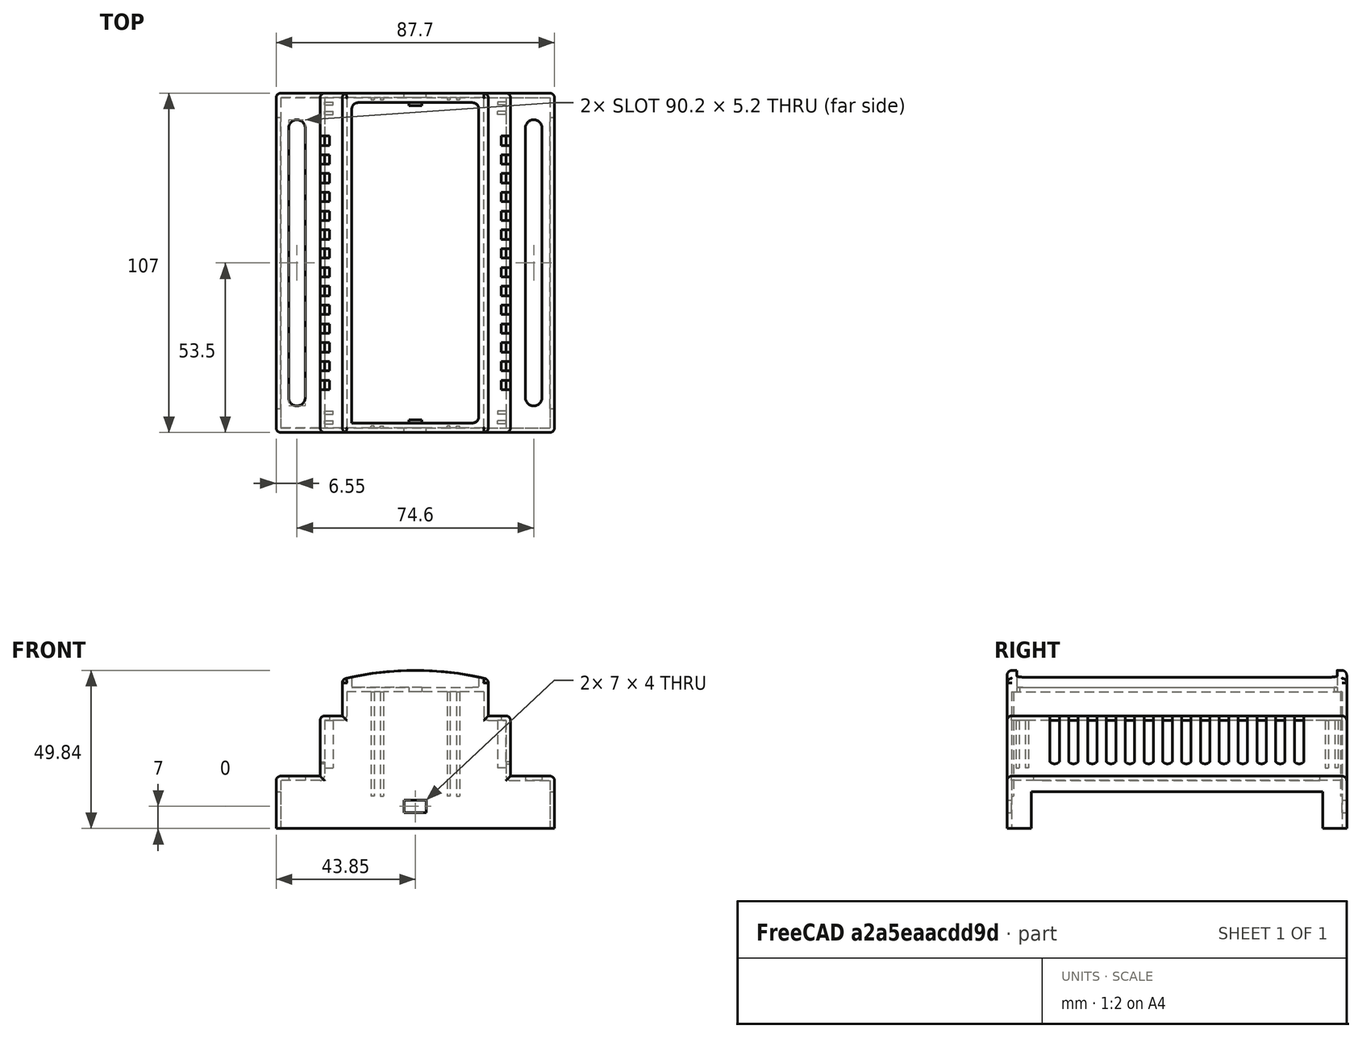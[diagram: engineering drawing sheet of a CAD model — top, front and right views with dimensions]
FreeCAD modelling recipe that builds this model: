
FCSTD DOCUMENT  (FreeCAD 1.0R39285 (Git))
Label: Diseño superior de la pieza (2023-1283)
License: All rights reserved
LicenseURL: https://en.wikipedia.org/wiki/All_rights_reserved
objects: Sketcher::SketchObject×15, PartDesign::Pad×9, PartDesign::Mirrored×7, PartDesign::Pocket×6, PartDesign::Fillet×4, PartDesign::Thickness×2, PartDesign::Plane×1, PartDesign::Body×1
note: 109 computed .brp shape members not serialized (recipe doc carries the construction recipe); baked Part::Feature solids carry a one-line shape summary decoded from their .brp

FEATURE [Sketcher::SketchObject] Sketch
  ArcFitTolerance = 1e-06
  AttachmentSupport = -> [XZ_Plane001]
  FullyConstrained = true
  MakeInternals = false
  MapMode = 5
  Placement = pos=(0,0,0) rot=(1,0,0;1.5708rad)
  sketch-geometry (12):
    g0: LineSegment StartX=-43.85 StartY=0 StartZ=0 EndX=43.85 EndY=0 EndZ=0
    g1: LineSegment StartX=-43.85 StartY=0 StartZ=0 EndX=-43.85 EndY=16.54 EndZ=0
    g2: LineSegment StartX=43.85 StartY=0 StartZ=0 EndX=43.85 EndY=16.54 EndZ=0
    g3: LineSegment StartX=-43.85 StartY=16.54 StartZ=0 EndX=-30 EndY=16.54 EndZ=0
    g4: LineSegment StartX=43.85 StartY=16.54 StartZ=0 EndX=30 EndY=16.54 EndZ=0
    g5: LineSegment StartX=-30 StartY=16.54 StartZ=0 EndX=-30 EndY=35.54 EndZ=0
    g6: LineSegment StartX=30 StartY=16.54 StartZ=0 EndX=30 EndY=35.54 EndZ=0
    g7: LineSegment StartX=-30 StartY=35.54 StartZ=0 EndX=-23 EndY=35.54 EndZ=0
    g8: LineSegment StartX=30 StartY=35.54 StartZ=0 EndX=23 EndY=35.54 EndZ=0
    g9: LineSegment StartX=23 StartY=35.54 StartZ=0 EndX=23 EndY=44.54 EndZ=0
    g10: LineSegment StartX=-23 StartY=35.54 StartZ=0 EndX=-23 EndY=44.54 EndZ=0
    g11: LineSegment StartX=-23 StartY=44.54 StartZ=0 EndX=23 EndY=44.54 EndZ=0
  constraints (36):
    c: Distance(g0) = 87.7
    c: PointOnObject(g0,g-1)
    c: PointOnObject(g0,g-1)
    c: Vertical(g1)
    c: Coincident(g1,g0)
    c: Vertical(g2)
    c: Coincident(g2,g0)
    c: Distance(g3) = 13.85
    c: Horizontal(g3)
    c: Coincident(g3,g1)
    c: Distance(g4) = 13.85
    c: Horizontal(g4)
    c: Coincident(g4,g2)
    c: Vertical(g5)
    c: Coincident(g5,g3)
    c: Vertical(g6)
    c: Coincident(g6,g4)
    c: Distance(g7) = 7
    c: Horizontal(g7)
    c: Coincident(g7,g5)
    c: Distance(g8) = 7
    c: Horizontal(g8)
    c: Coincident(g8,g6)
    c: Vertical(g9)
    c: Coincident(g9,g8)
    c: Vertical(g10)
    c: Coincident(g10,g7)
    c: Coincident(g11,g10)
    c: Coincident(g11,g9)
    c: Equal(g1,g2)
    c: Equal(g5,g6)
    c: Equal(g10,g9)
    c: Distance(g0,g11) = 44.54
    c: DistanceY(g1,g1) = 16.54
    c: Distance(g5,g0) = 35.54
    c: Distance(g10,g-2) = 23
FEATURE [PartDesign::Pad] Pad
  Direction = (0,-1,2e-16)
  Length = 107
  Length2 = 10
  Placement = pos=(0,0,0) rot=(1,0,0;1.5708rad)
  Profile = -> Sketch
  ReferenceAxis = -> Sketch [N_Axis]
  Refine = true
  Suppressed = false
  Type = 0
FEATURE [PartDesign::Thickness] Thickness
  Base = -> Pad
  BaseFeature = -> Pad
  Intersection = false
  Join = 0
  Mode = 0
  Placement = pos=(0,0,0) rot=(1,0,0;1.5708rad)
  Refine = true
  Reversed = true
  SupportTransform = false
  Suppressed = false
  Value = 1.4
FEATURE [PartDesign::Thickness] Thickness001
  Base = -> Thickness [Face1]
  BaseFeature = -> Thickness
  Intersection = false
  Join = 0
  Mode = 0
  Refine = true
  Reversed = true
  SupportTransform = false
  Suppressed = false
  Value = 1.4
FEATURE [Sketcher::SketchObject] Sketch001
  ArcFitTolerance = 1e-06
  AttachmentSupport = -> [Thickness001]
  FullyConstrained = true
  MakeInternals = false
  MapMode = 5
  Placement = pos=(-43.85,0,0) rot=(0.57735,-0.57735,-0.57735;2.0944rad)
  sketch-geometry (4):
    g0: LineSegment StartX=7.575 StartY=0 StartZ=0 EndX=99.425 EndY=0 EndZ=0
    g1: LineSegment StartX=99.425 StartY=0 StartZ=0 EndX=99.425 EndY=11.6 EndZ=0
    g2: LineSegment StartX=99.425 StartY=11.6 StartZ=0 EndX=7.575 EndY=11.6 EndZ=0
    g3: LineSegment StartX=7.575 StartY=11.6 StartZ=0 EndX=7.575 EndY=0 EndZ=0
  constraints (12):
    c: Coincident(g0,g1)
    c: Coincident(g1,g2)
    c: Coincident(g2,g3)
    c: Coincident(g3,g0)
    c: Horizontal(g0)
    c: Horizontal(g2)
    c: Vertical(g1)
    c: Vertical(g3)
    c: PointOnObject(g0,g-1)
    c: DistanceX(g2,g2) = 91.85
    c: DistanceY(g1,g1) = 11.6
    c: DistanceX(g-1,g0) = 7.575
FEATURE [PartDesign::Pocket] Pocket
  BaseFeature = -> Thickness001
  Direction = (1,0,0)
  Length = 5
  Length2 = 5
  Profile = -> Sketch001
  ReferenceAxis = -> Sketch001 [N_Axis]
  Refine = true
  Suppressed = false
  Type = 1
FEATURE [Sketcher::SketchObject] Sketch002
  ArcFitTolerance = 1e-06
  AttachmentSupport = -> [Pocket]
  FullyConstrained = true
  MakeInternals = false
  MapMode = 5
  Placement = pos=(0,4.2e-15,0) rot=(0,0.707107,0.707107;3.14159rad)
  sketch-geometry (4):
    g0: LineSegment StartX=-23 StartY=44.54 StartZ=0 EndX=23 EndY=44.54 EndZ=0
    g1: LineSegment StartX=-23 StartY=44.54 StartZ=0 EndX=-23 EndY=47.04 EndZ=0
    g2: LineSegment StartX=23 StartY=44.54 StartZ=0 EndX=23 EndY=47.04 EndZ=0
    g3: ArcOfCircle CenterX=1.7e-15 CenterY=-46.0243 CenterZ=0 NormalX=0 NormalY=0 NormalZ=1 AngleXU=0 Radius=95.8643 StartAngle=1.32851 EndAngle=1.81308
  constraints (13):
    c: Distance(g0) = 46
    c: Horizontal(g0)
    c: Distance(g-1,g0) = 44.54
    c: Distance(g0,g-2) = 23
    c: Distance(g1) = 2.5
    c: Coincident(g1,g0)
    c: Vertical(g1)
    c: Distance(g2) = 2.5
    c: Coincident(g2,g0)
    c: Vertical(g2)
    c: Coincident(g3,g1)
    c: Coincident(g3,g2)
    c: Distance(g3,g0) = -5.3
FEATURE [PartDesign::Pad] Pad001
  BaseFeature = -> Pocket
  Direction = (0,1,-2e-16)
  Length = 107
  Length2 = 10
  Profile = -> Sketch002
  ReferenceAxis = -> Sketch002 [N_Axis]
  Refine = true
  Suppressed = false
  Type = 0
FEATURE [Sketcher::SketchObject] Sketch003
  ArcFitTolerance = 1e-06
  AttachmentSupport = -> [Pad001]
  ExternalGeometry = -> [Pad001]
  FullyConstrained = true
  MakeInternals = false
  MapMode = 5
  Placement = pos=(0,4.2e-15,0) rot=(0,0.707107,0.707107;3.14159rad)
  sketch-geometry (4):
    g0: LineSegment StartX=-23 StartY=44.54 StartZ=0 EndX=-23 EndY=47.04 EndZ=0
    g1: LineSegment StartX=23 StartY=44.54 StartZ=0 EndX=23 EndY=47.04 EndZ=0
    g2: ArcOfCircle CenterX=4.82e-14 CenterY=-46.0243 CenterZ=0 NormalX=0 NormalY=0 NormalZ=1 AngleXU=0 Radius=95.8643 StartAngle=1.32851 EndAngle=1.81308
    g3: LineSegment StartX=-23 StartY=44.54 StartZ=0 EndX=23 EndY=44.54 EndZ=0
  constraints (9):
    c: Distance(g0) = 2.5
    c: Coincident(g2,g0)
    c: Coincident(g2,g1)
    c: Coincident(g3,g-3)
    c: Coincident(g3,g-3)
    c: Perpendicular(g0,g3) = 4.71239
    c: Distance(g2,g3) = -5.3
    c: Perpendicular(g1,g3) = 4.71239
    c: DistanceY(g1,g1) = 2.5
FEATURE [PartDesign::Pad] Pad002
  BaseFeature = -> Pad001
  Direction = (0,1,-2e-16)
  Length = 3
  Length2 = 10
  Profile = -> Sketch003
  ReferenceAxis = -> Sketch003 [N_Axis]
  Refine = true
  Reversed = true
  Suppressed = false
  Type = 0
FEATURE [Sketcher::SketchObject] Sketch004
  ArcFitTolerance = 1e-06
  AttachmentSupport = -> [Pad002]
  ExternalGeometry = -> [Pad002]
  FullyConstrained = true
  MakeInternals = false
  MapMode = 5
  Placement = pos=(0,-107,0) rot=(1,0,0;1.5708rad)
  sketch-geometry (4):
    g0: LineSegment StartX=-23 StartY=44.54 StartZ=0 EndX=23 EndY=44.54 EndZ=0
    g1: LineSegment StartX=23 StartY=44.54 StartZ=0 EndX=23 EndY=47.04 EndZ=0
    g2: LineSegment StartX=-23 StartY=44.54 StartZ=0 EndX=-23 EndY=47.04 EndZ=0
    g3: ArcOfCircle CenterX=3.7756e-12 CenterY=-46.0243 CenterZ=0 NormalX=0 NormalY=0 NormalZ=1 AngleXU=0 Radius=95.8643 StartAngle=1.32851 EndAngle=1.81308
  constraints (9):
    c: Coincident(g0,g-5)
    c: Coincident(g0,g-6)
    c: Coincident(g1,g0)
    c: Coincident(g1,g-6)
    c: Coincident(g2,g0)
    c: Coincident(g2,g-5)
    c: Coincident(g3,g2)
    c: Coincident(g3,g1)
    c: Tangent(g3,g-4)
FEATURE [PartDesign::Pad] Pad003
  BaseFeature = -> Pad002
  Direction = (0,-1,2e-16)
  Length = 3
  Length2 = 10
  Profile = -> Sketch004
  ReferenceAxis = -> Sketch004 [N_Axis]
  Refine = true
  Reversed = true
  Suppressed = false
  Type = 0
FEATURE [Sketcher::SketchObject] Sketch005
  ArcFitTolerance = 1e-06
  AttachmentSupport = -> [Pad003]
  ExternalGeometry = -> [Pad003]
  FullyConstrained = true
  MakeInternals = false
  MapMode = 5
  Placement = pos=(23,-8.5e-15,1.304e-13) rot=(0.57735,0.57735,0.57735;2.0944rad)
  sketch-geometry (4):
    g0: LineSegment StartX=-104 StartY=49.84 StartZ=0 EndX=-104 EndY=44.54 EndZ=0
    g1: LineSegment StartX=-104 StartY=44.54 StartZ=0 EndX=-3 EndY=44.54 EndZ=0
    g2: LineSegment StartX=-3 StartY=49.84 StartZ=0 EndX=-3 EndY=44.54 EndZ=0
    g3: LineSegment StartX=-104 StartY=49.84 StartZ=0 EndX=-3 EndY=49.84 EndZ=0
  constraints (8):
    c: Coincident(g0,g-5)
    c: Coincident(g0,g-3)
    c: Coincident(g1,g0)
    c: Coincident(g1,g-3)
    c: Coincident(g2,g-4)
    c: Coincident(g2,g1)
    c: Coincident(g3,g0)
    c: Coincident(g3,g2)
FEATURE [PartDesign::Pad] Pad004
  BaseFeature = -> Pad003
  Direction = (1,0,5.8e-15)
  Length = 3
  Length2 = 10
  Profile = -> Sketch005
  ReferenceAxis = -> Sketch005 [N_Axis]
  Refine = true
  Reversed = true
  Suppressed = false
  Type = 0
FEATURE [PartDesign::Mirrored] Mirrored
  BaseFeature = -> Pad004
  MirrorPlane = -> YZ_Plane001
  Originals = -> [Pad004]
  Refine = true
  Suppressed = false
  TransformMode = 0
FEATURE [Sketcher::SketchObject] Sketch006
  ArcFitTolerance = 1e-06
  AttachmentSupport = -> [Mirrored]
  FullyConstrained = true
  MakeInternals = false
  MapMode = 5
  Placement = pos=(0,7.3e-15,16.54) rot=(0,0,1;0rad)
  sketch-geometry (4):
    g0: ArcOfCircle CenterX=37.3 CenterY=-11 CenterZ=0 NormalX=0 NormalY=0 NormalZ=1 AngleXU=0 Radius=2.6 StartAngle=2.2037e-12 EndAngle=3.14159
    g1: ArcOfCircle CenterX=37.3 CenterY=-96 CenterZ=0 NormalX=0 NormalY=0 NormalZ=1 AngleXU=0 Radius=2.6 StartAngle=3.14159 EndAngle=6.28319
    g2: LineSegment StartX=39.9 StartY=-11 StartZ=0 EndX=39.9 EndY=-96 EndZ=0
    g3: LineSegment StartX=34.7 StartY=-11 StartZ=0 EndX=34.7 EndY=-96 EndZ=0
  constraints (10):
    c: Tangent(g0,g2) = 1.5708
    c: Tangent(g0,g3) = -1.5708
    c: Tangent(g1,g2) = 1.5708
    c: Tangent(g1,g3) = -1.5708
    c: Equal(g0,g1)
    c: Vertical(g2)
    c: Distance(g2,g3) = 5.2
    c: DistanceY(g2,g2) = 85
    c: Distance(g0,g-2) = 37.3
    c: Distance(g0,g-1) = 11
FEATURE [PartDesign::Pocket] Pocket001
  BaseFeature = -> Mirrored
  Direction = (0,0,-1)
  Length = 5
  Length2 = 5
  Profile = -> Sketch006
  ReferenceAxis = -> Sketch006 [N_Axis]
  Refine = true
  Suppressed = false
  Type = 0
FEATURE [PartDesign::Mirrored] Mirrored001
  BaseFeature = -> Pocket001
  MirrorPlane = -> YZ_Plane001
  Originals = -> [Pocket001]
  Refine = true
  Suppressed = false
  TransformMode = 0
FEATURE [Sketcher::SketchObject] Sketch007
  ArcFitTolerance = 1e-06
  AttachmentSupport = -> [Mirrored001]
  ExternalGeometry = -> [Mirrored001]
  FullyConstrained = true
  MakeInternals = false
  MapMode = 5
  Placement = pos=(30,0,0) rot=(0.57735,0.57735,0.57735;2.0944rad)
  sketch-geometry (57):
    g0: LineSegment [constr] StartX=-53.5 StartY=35.54 StartZ=0 EndX=-53.5 EndY=16.54 EndZ=0
    g1: LineSegment StartX=-16.4625 StartY=35.54 StartZ=0 EndX=-13.4995 EndY=35.54 EndZ=0
    g2: LineSegment StartX=-13.4995 StartY=35.54 StartZ=0 EndX=-13.4995 EndY=21.04 EndZ=0
    g3: LineSegment StartX=-16.4625 StartY=35.54 StartZ=0 EndX=-16.4625 EndY=21.04 EndZ=0
    g4: ArcOfCircle CenterX=-14.981 CenterY=22.3836 CenterZ=0 NormalX=0 NormalY=0 NormalZ=1 AngleXU=0 Radius=2 StartAngle=3.8782 EndAngle=5.54658
    g5: LineSegment StartX=-22.3885 StartY=35.54 StartZ=0 EndX=-19.4255 EndY=35.54 EndZ=0
    g6: LineSegment StartX=-19.4255 StartY=35.54 StartZ=0 EndX=-19.4255 EndY=21.04 EndZ=0
    g7: LineSegment StartX=-22.3885 StartY=35.54 StartZ=0 EndX=-22.3885 EndY=21.04 EndZ=0
    g8: ArcOfCircle CenterX=-20.907 CenterY=22.3836 CenterZ=0 NormalX=0 NormalY=0 NormalZ=1 AngleXU=0 Radius=2 StartAngle=3.8782 EndAngle=5.54658
    g9: LineSegment StartX=-28.3145 StartY=35.54 StartZ=0 EndX=-25.3515 EndY=35.54 EndZ=0
    g10: LineSegment StartX=-25.3515 StartY=35.54 StartZ=0 EndX=-25.3515 EndY=21.04 EndZ=0
    g11: LineSegment StartX=-28.3145 StartY=35.54 StartZ=0 EndX=-28.3145 EndY=21.04 EndZ=0
    g12: ArcOfCircle CenterX=-26.833 CenterY=22.3836 CenterZ=0 NormalX=0 NormalY=0 NormalZ=1 AngleXU=0 Radius=2 StartAngle=3.8782 EndAngle=5.54658
    g13: LineSegment StartX=-34.2405 StartY=35.54 StartZ=0 EndX=-31.2775 EndY=35.54 EndZ=0
    g14: LineSegment StartX=-34.2405 StartY=35.54 StartZ=0 EndX=-34.2405 EndY=21.04 EndZ=0
    g15: LineSegment StartX=-31.2775 StartY=35.54 StartZ=0 EndX=-31.2775 EndY=21.04 EndZ=0
    g16: ArcOfCircle CenterX=-32.759 CenterY=22.3836 CenterZ=0 NormalX=0 NormalY=0 NormalZ=1 AngleXU=0 Radius=2 StartAngle=3.8782 EndAngle=5.54658
    g17: LineSegment StartX=-40.1665 StartY=35.54 StartZ=0 EndX=-37.2035 EndY=35.54 EndZ=0
    g18: LineSegment StartX=-37.2035 StartY=35.54 StartZ=0 EndX=-37.2035 EndY=21.04 EndZ=0
    g19: LineSegment StartX=-40.1665 StartY=35.54 StartZ=0 EndX=-40.1665 EndY=21.04 EndZ=0
    g20: ArcOfCircle CenterX=-38.685 CenterY=22.3836 CenterZ=0 NormalX=0 NormalY=0 NormalZ=1 AngleXU=0 Radius=2 StartAngle=3.8782 EndAngle=5.54658
    g21: LineSegment StartX=-46.0925 StartY=35.54 StartZ=0 EndX=-43.1295 EndY=35.54 EndZ=0
    g22: LineSegment StartX=-43.1295 StartY=35.54 StartZ=0 EndX=-43.1295 EndY=21.04 EndZ=0
    g23: LineSegment StartX=-46.0925 StartY=35.54 StartZ=0 EndX=-46.0925 EndY=21.04 EndZ=0
    g24: ArcOfCircle CenterX=-44.611 CenterY=22.3836 CenterZ=0 NormalX=0 NormalY=0 NormalZ=1 AngleXU=0 Radius=2 StartAngle=3.8782 EndAngle=5.54658
    g25: LineSegment StartX=-52.0185 StartY=35.54 StartZ=0 EndX=-49.0555 EndY=35.54 EndZ=0
    g26: LineSegment StartX=-49.0555 StartY=35.54 StartZ=0 EndX=-49.0555 EndY=21.04 EndZ=0
    g27: LineSegment StartX=-52.0185 StartY=35.54 StartZ=0 EndX=-52.0185 EndY=21.04 EndZ=0
    g28: ArcOfCircle CenterX=-50.537 CenterY=22.3836 CenterZ=0 NormalX=0 NormalY=0 NormalZ=1 AngleXU=0 Radius=2 StartAngle=3.8782 EndAngle=5.54658
    g29: LineSegment StartX=-57.9445 StartY=35.54 StartZ=0 EndX=-54.9815 EndY=35.54 EndZ=0
    g30: LineSegment StartX=-54.9815 StartY=35.54 StartZ=0 EndX=-54.9815 EndY=21.04 EndZ=0
    g31: LineSegment StartX=-57.9445 StartY=35.54 StartZ=0 EndX=-57.9445 EndY=21.04 EndZ=0
    g32: ArcOfCircle CenterX=-56.463 CenterY=22.3836 CenterZ=0 NormalX=0 NormalY=0 NormalZ=1 AngleXU=0 Radius=2 StartAngle=3.8782 EndAngle=5.54658
    g33: LineSegment StartX=-63.8705 StartY=35.54 StartZ=0 EndX=-60.9075 EndY=35.54 EndZ=0
    g34: LineSegment StartX=-60.9075 StartY=35.54 StartZ=0 EndX=-60.9075 EndY=21.04 EndZ=0
    g35: LineSegment StartX=-63.8705 StartY=35.54 StartZ=0 EndX=-63.8705 EndY=21.04 EndZ=0
    g36: ArcOfCircle CenterX=-62.389 CenterY=22.3836 CenterZ=0 NormalX=0 NormalY=0 NormalZ=1 AngleXU=0 Radius=2 StartAngle=3.8782 EndAngle=5.54658
    g37: LineSegment StartX=-69.7965 StartY=35.54 StartZ=0 EndX=-66.8335 EndY=35.54 EndZ=0
    g38: LineSegment StartX=-66.8335 StartY=35.54 StartZ=0 EndX=-66.8335 EndY=21.04 EndZ=0
    g39: LineSegment StartX=-69.7965 StartY=35.54 StartZ=0 EndX=-69.7965 EndY=21.04 EndZ=0
    g40: ArcOfCircle CenterX=-68.315 CenterY=22.3836 CenterZ=0 NormalX=0 NormalY=0 NormalZ=1 AngleXU=0 Radius=2 StartAngle=3.8782 EndAngle=5.54658
    g41: LineSegment StartX=-75.7225 StartY=35.54 StartZ=0 EndX=-72.7595 EndY=35.54 EndZ=0
    g42: LineSegment StartX=-72.7595 StartY=35.54 StartZ=0 EndX=-72.7595 EndY=21.04 EndZ=0
    g43: LineSegment StartX=-75.7225 StartY=35.54 StartZ=0 EndX=-75.7225 EndY=21.04 EndZ=0
    g44: ArcOfCircle CenterX=-74.241 CenterY=22.3836 CenterZ=0 NormalX=0 NormalY=0 NormalZ=1 AngleXU=0 Radius=2 StartAngle=3.8782 EndAngle=5.54658
    g45: LineSegment StartX=-81.6485 StartY=35.54 StartZ=0 EndX=-78.6855 EndY=35.54 EndZ=0
    g46: LineSegment StartX=-78.6855 StartY=35.54 StartZ=0 EndX=-78.6855 EndY=21.04 EndZ=0
    g47: LineSegment StartX=-81.6485 StartY=35.54 StartZ=0 EndX=-81.6485 EndY=21.04 EndZ=0
    g48: ArcOfCircle CenterX=-80.167 CenterY=22.3836 CenterZ=0 NormalX=0 NormalY=0 NormalZ=1 AngleXU=0 Radius=2 StartAngle=3.8782 EndAngle=5.54658
    g49: LineSegment StartX=-87.5745 StartY=35.54 StartZ=0 EndX=-84.6115 EndY=35.54 EndZ=0
    g50: LineSegment StartX=-84.6115 StartY=35.54 StartZ=0 EndX=-84.6115 EndY=21.04 EndZ=0
    g51: LineSegment StartX=-87.5745 StartY=35.54 StartZ=0 EndX=-87.5745 EndY=21.04 EndZ=0
    g52: ArcOfCircle CenterX=-86.093 CenterY=22.3836 CenterZ=0 NormalX=0 NormalY=0 NormalZ=1 AngleXU=0 Radius=2 StartAngle=3.8782 EndAngle=5.54658
    g53: LineSegment StartX=-93.5005 StartY=35.54 StartZ=0 EndX=-90.5375 EndY=35.54 EndZ=0
    g54: LineSegment StartX=-90.5375 StartY=35.54 StartZ=0 EndX=-90.5375 EndY=21.04 EndZ=0
    g55: LineSegment StartX=-93.5005 StartY=35.54 StartZ=0 EndX=-93.5005 EndY=21.04 EndZ=0
    g56: ArcOfCircle CenterX=-92.019 CenterY=22.3836 CenterZ=0 NormalX=0 NormalY=0 NormalZ=1 AngleXU=0 Radius=2 StartAngle=3.8782 EndAngle=5.54658
  constraints (184):
    c: Symmetric(g-4,g-4,g0)
    c: Symmetric(g-3,g-3,g0)
    c: PointOnObject(g1,g-4)
    c: PointOnObject(g1,g-4)
    c: Distance(g2) = 14.5
    c: Vertical(g2)
    c: Coincident(g2,g1)
    c: Vertical(g3)
    c: Coincident(g3,g1)
    c: Coincident(g4,g3)
    c: Coincident(g4,g2)
    c: DistanceX(g1,g1) = 2.963
    c: Radius(g4) = 2
    c: Distance(g5) = 2.963
    c: Horizontal(g5)
    c: PointOnObject(g5,g-4)
    c: Vertical(g6)
    c: Coincident(g6,g5)
    c: Vertical(g7)
    c: Coincident(g7,g5)
    c: Equal(g2,g3)
    c: Equal(g3,g6)
    c: Equal(g6,g7)
    c: Distance(g3,g6) = 2.963
    c: Coincident(g8,g7)
    c: Coincident(g8,g6)
    c: Equal(g4,g8)
    c: Horizontal(g9)
    c: PointOnObject(g9,g-4)
    c: Vertical(g10)
    c: Coincident(g10,g9)
    c: Vertical(g11)
    c: Coincident(g11,g9)
    c: Coincident(g12,g11)
    c: Coincident(g12,g10)
    c: Equal(g5,g9)
    c: Equal(g6,g10)
    c: Equal(g10,g11)
    c: Equal(g4,g12)
    c: Distance(g7,g10) = 2.963
    c: PointOnObject(g13,g-4)
    c: PointOnObject(g13,g-4)
    c: Vertical(g14)
    c: Coincident(g14,g13)
    c: Vertical(g15)
    c: Coincident(g15,g13)
    c: Coincident(g16,g14)
    c: Coincident(g16,g15)
    c: Equal(g15,g14)
    c: Equal(g14,g2)
    c: Equal(g1,g13)
    c: Distance(g11,g15) = 2.963
    c: Equal(g4,g16)
    c: PointOnObject(g17,g-4)
    c: PointOnObject(g17,g-4)
    c: Vertical(g18)
    c: Coincident(g18,g17)
    c: Vertical(g19)
    c: Coincident(g19,g17)
    c: Coincident(g20,g19)
    c: Coincident(g20,g18)
    c: Distance(g14,g18) = 2.963
    c: Equal(g2,g18)
    c: Equal(g18,g19)
    c: Equal(g1,g17)
    c: Equal(g4,g20)
    c: PointOnObject(g21,g-4)
    c: PointOnObject(g21,g-4)
    c: Vertical(g22)
    c: Coincident(g22,g21)
    c: Vertical(g23)
    c: Coincident(g23,g21)
    c: Coincident(g24,g23)
    c: Coincident(g24,g22)
    c: Equal(g1,g21)
    c: Equal(g22,g23)
    c: Equal(g23,g2)
    c: Distance(g19,g22) = 2.963
    c: Equal(g4,g24)
    c: PointOnObject(g25,g-4)
    c: PointOnObject(g25,g-4)
    c: Vertical(g26)
    c: Coincident(g26,g25)
    c: Vertical(g27)
    c: Coincident(g27,g25)
    c: Coincident(g28,g27)
    c: Coincident(g28,g26)
    c: Equal(g2,g26)
    c: Equal(g26,g27)
    c: Equal(g1,g25)
    c: Equal(g4,g28)
    c: Distance(g23,g26) = 2.963
    c: PointOnObject(g29,g-4)
    c: PointOnObject(g29,g-4)
    c: Coincident(g30,g29)
    c: Vertical(g30)
    c: Coincident(g31,g29)
    c: Vertical(g31)
    c: Equal(g30,g31)
    c: Equal(g31,g3)
    c: Coincident(g32,g31)
    c: Coincident(g32,g30)
    c: Equal(g4,g32)
    c: Equal(g29,g1)
    c: Distance(g27,g30) = 2.963
    c: PointOnObject(g33,g-4)
    c: PointOnObject(g33,g-4)
    c: Coincident(g34,g33)
    c: Vertical(g34)
    c: Coincident(g35,g33)
    c: Vertical(g35)
    c: Equal(g35,g34)
    c: Equal(g34,g31)
    c: Equal(g33,g29)
    c: Coincident(g36,g35)
    c: Coincident(g36,g34)
    c: Equal(g32,g36)
    c: Distance(g31,g34) = 2.963
    c: PointOnObject(g37,g-4)
    c: PointOnObject(g37,g-4)
    c: Coincident(g38,g37)
    c: Vertical(g38)
    c: Coincident(g39,g37)
    c: Vertical(g39)
    c: Coincident(g40,g39)
    c: Coincident(g40,g38)
    c: Equal(g38,g39)
    c: Equal(g39,g35)
    c: Equal(g40,g36)
    c: Equal(g33,g37)
    c: Distance(g35,g38) = 2.963
    c: PointOnObject(g41,g-4)
    c: PointOnObject(g41,g-4)
    c: Coincident(g42,g41)
    c: Vertical(g42)
    c: Coincident(g43,g41)
    c: Vertical(g43)
    c: Coincident(g44,g43)
    c: Coincident(g44,g42)
    c: Equal(g43,g42)
    c: Equal(g42,g39)
    c: Equal(g41,g37)
    c: Equal(g44,g40)
    c: Distance(g39,g42) = 2.963
    c: PointOnObject(g45,g-4)
    c: PointOnObject(g45,g-4)
    c: Coincident(g46,g45)
    c: Vertical(g46)
    c: Coincident(g47,g45)
    c: Vertical(g47)
    c: Coincident(g48,g47)
    c: Coincident(g48,g46)
    c: Equal(g47,g46)
    c: Equal(g46,g43)
    c: Equal(g45,g41)
    c: Equal(g44,g48)
    c: Distance(g43,g46) = 2.963
    c: PointOnObject(g49,g-4)
    c: PointOnObject(g49,g-4)
    c: Coincident(g50,g49)
    c: Vertical(g50)
    c: Coincident(g51,g49)
    c: Vertical(g51)
    c: Coincident(g52,g51)
    c: Coincident(g52,g50)
    c: Equal(g51,g50)
    c: Equal(g50,g47)
    c: Equal(g49,g45)
    c: Equal(g48,g52)
    c: Distance(g47,g50) = 2.963
    c: PointOnObject(g53,g-4)
    c: PointOnObject(g53,g-4)
    c: Coincident(g54,g53)
    c: Vertical(g54)
    c: Coincident(g55,g53)
    c: Vertical(g55)
    c: Coincident(g56,g55)
    c: Coincident(g56,g54)
    c: Equal(g55,g54)
    c: Equal(g54,g51)
    c: Equal(g56,g52)
    c: Equal(g53,g49)
    c: Distance(g51,g54) = 2.963
    c: Distance(g0,g27) = 1.4815
FEATURE [PartDesign::Pocket] Pocket002
  BaseFeature = -> Mirrored001
  Direction = (-1,0,0)
  Length = 2.963
  Length2 = 5
  Profile = -> Sketch007
  ReferenceAxis = -> Sketch007 [N_Axis]
  Refine = true
  Suppressed = false
  Type = 0
FEATURE [PartDesign::Mirrored] Mirrored002
  BaseFeature = -> Pocket002
  MirrorPlane = -> YZ_Plane001
  Originals = -> [Pocket002]
  Refine = true
  Suppressed = false
  TransformMode = 0
FEATURE [PartDesign::Fillet] Fillet
  Base = -> Mirrored002 [Edge272,Edge110,Edge99,Edge166,Edge114,Edge118,Edge122,Edge126,Edge130,Edge134,Edge138,Edge142,Edge146,Edge150,Edge154,Edge158,Edge162,Edge20,Edge98,Edge97,Edge96]
  BaseFeature = -> Mirrored002
  Radius = 1.5
  Refine = true
  SupportTransform = false
  Suppressed = false
  UseAllEdges = false
FEATURE [PartDesign::Mirrored] Mirrored003
  BaseFeature = -> Fillet
  MirrorPlane = -> YZ_Plane001
  Originals = -> [Fillet]
  Refine = true
  Suppressed = false
  TransformMode = 0
FEATURE [Sketcher::SketchObject] Sketch008
  ArcFitTolerance = 1e-06
  AttachmentSupport = -> [Mirrored003]
  FullyConstrained = true
  MakeInternals = false
  MapMode = 5
  Placement = pos=(0,-107,3.53e-14) rot=(1,0,0;1.5708rad)
  sketch-geometry (4):
    g0: LineSegment StartX=-3.5 StartY=9 StartZ=0 EndX=3.5 EndY=9 EndZ=0
    g1: LineSegment StartX=-3.5 StartY=9 StartZ=0 EndX=-3.5 EndY=5 EndZ=0
    g2: LineSegment StartX=3.5 StartY=9 StartZ=0 EndX=3.5 EndY=5 EndZ=0
    g3: LineSegment StartX=-3.5 StartY=5 StartZ=0 EndX=3.5 EndY=5 EndZ=0
  constraints (12):
    c: Distance(g0) = 7
    c: Horizontal(g0)
    c: Vertical(g1)
    c: Coincident(g1,g0)
    c: Distance(g2) = 4
    c: Vertical(g2)
    c: Coincident(g2,g0)
    c: Coincident(g3,g1)
    c: Coincident(g3,g2)
    c: Distance(g-2,g1) = 3.5
    c: Equal(g2,g1)
    c: Distance(g-1,g3) = 5
FEATURE [PartDesign::Pocket] Pocket003
  BaseFeature = -> Mirrored003
  Direction = (0,1,-2e-16)
  Length = 5
  Length2 = 5
  Profile = -> Sketch008
  ReferenceAxis = -> Sketch008 [N_Axis]
  Refine = true
  Suppressed = false
  Type = 1
FEATURE [Sketcher::SketchObject] Sketch009
  ArcFitTolerance = 1e-06
  AttachmentSupport = -> [Pocket003]
  ExternalGeometry = -> [Pocket003]
  FullyConstrained = true
  MakeInternals = false
  MapMode = 5
  Placement = pos=(0,-104,0) rot=(1,0,0;1.5708rad)
  sketch-geometry (8):
    g0: LineSegment StartX=-23 StartY=47.04 StartZ=0 EndX=-23 EndY=49.84 EndZ=0
    g1: LineSegment StartX=-23 StartY=49.84 StartZ=0 EndX=-20 EndY=49.84 EndZ=0
    g2: LineSegment StartX=-20 StartY=49.84 StartZ=0 EndX=-20 EndY=47.7305 EndZ=0
    g3: ArcOfCircle CenterX=9.71783e-05 CenterY=-46.0247 CenterZ=0 NormalX=0 NormalY=0 NormalZ=1 AngleXU=0 Radius=95.8647 StartAngle=1.78097 EndAngle=1.81308
    g4: LineSegment StartX=20 StartY=49.84 StartZ=0 EndX=23 EndY=49.84 EndZ=0
    g5: LineSegment StartX=23 StartY=49.84 StartZ=0 EndX=23 EndY=47.04 EndZ=0
    g6: LineSegment StartX=20 StartY=49.84 StartZ=0 EndX=20 EndY=47.7305 EndZ=0
    g7: ArcOfCircle CenterX=-7.58465e-05 CenterY=-46.0246 CenterZ=0 NormalX=0 NormalY=0 NormalZ=1 AngleXU=0 Radius=95.8646 StartAngle=1.32851 EndAngle=1.36062
  constraints (19):
    c: Coincident(g0,g-6)
    c: Coincident(g0,g-6)
    c: Coincident(g1,g0)
    c: Coincident(g1,g-5)
    c: Coincident(g2,g1)
    c: Coincident(g2,g-4)
    c: Coincident(g3,g0)
    c: Coincident(g3,g2)
    c: Tangent(g3,g-3)
    c: Coincident(g4,g-8)
    c: Coincident(g4,g-9)
    c: Coincident(g5,g4)
    c: PointOnObject(g5,g-10)
    c: Vertical(g5)
    c: Coincident(g6,g4)
    c: Coincident(g6,g-10)
    c: Coincident(g7,g6)
    c: Coincident(g7,g5)
    c: Tangent(g7,g-10)
FEATURE [PartDesign::Pocket] Pocket004
  BaseFeature = -> Pocket003
  Direction = (0,1,-2e-16)
  Length = 0
  Length2 = 5
  Profile = -> Sketch009
  ReferenceAxis = -> Sketch009 [N_Axis]
  Refine = true
  Suppressed = false
  Type = 3
  UpToFace = -> Pocket003 [Face89]
FEATURE [PartDesign::Mirrored] Mirrored004
  BaseFeature = -> Pocket004
  MirrorPlane = -> YZ_Plane001
  Originals = -> [Fillet]
  Refine = true
  Suppressed = false
  TransformMode = 0
FEATURE [PartDesign::Fillet] Fillet001
  Base = -> Mirrored004 [Edge26,Edge28,Edge32,Edge34,Edge33,Edge5,Edge22,Edge24,Edge25,Edge29]
  BaseFeature = -> Mirrored004
  Radius = 1.5
  Refine = true
  SupportTransform = false
  Suppressed = false
  UseAllEdges = false
FEATURE [Sketcher::SketchObject] Sketch010
  ArcFitTolerance = 1e-06
  FullyConstrained = true
  MakeInternals = false
  MapMode = 5
  Placement = pos=(0,1.96e-14,44.54) rot=(0,0,1;0rad)
  sketch-geometry (8):
    g0: LineSegment StartX=-2 StartY=-3 StartZ=0 EndX=2 EndY=-3 EndZ=0
    g1: LineSegment StartX=-2 StartY=-3 StartZ=0 EndX=-2 EndY=-4 EndZ=0
    g2: LineSegment StartX=2 StartY=-3 StartZ=0 EndX=2 EndY=-4 EndZ=0
    g3: LineSegment StartX=-2 StartY=-4 StartZ=0 EndX=2 EndY=-4 EndZ=0
    g4: LineSegment StartX=2 StartY=-104 StartZ=0 EndX=-2 EndY=-104 EndZ=0
    g5: LineSegment StartX=2 StartY=-104 StartZ=0 EndX=2 EndY=-103 EndZ=0
    g6: LineSegment StartX=-2 StartY=-104 StartZ=0 EndX=-2 EndY=-103 EndZ=0
    g7: LineSegment StartX=2 StartY=-103 StartZ=0 EndX=-2 EndY=-103 EndZ=0
  constraints (24):
    c: PointOnObject(g0,g-3)
    c: PointOnObject(g0,g-3)
    c: Distance(g1) = 1
    c: Vertical(g1)
    c: Coincident(g1,g0)
    c: Distance(g2) = 1
    c: Vertical(g2)
    c: Coincident(g2,g0)
    c: Coincident(g3,g1)
    c: Coincident(g3,g2)
    c: Distance(g-2,g1) = 2
    c: Distance(g0,g0) = 4
    c: PointOnObject(g4,g-4)
    c: PointOnObject(g4,g-4)
    c: Distance(g5) = 1
    c: Vertical(g5)
    c: Coincident(g5,g4)
    c: Distance(g6) = 1
    c: Vertical(g6)
    c: Coincident(g6,g4)
    c: Coincident(g7,g5)
    c: Coincident(g7,g6)
    c: Distance(g-2,g5) = 2
    c: DistanceX(g4,g4) = 4
FEATURE [PartDesign::Pocket] Pocket005
  BaseFeature = -> Fillet001
  Direction = (0,0,-1)
  Length = 5
  Length2 = 5
  Profile = -> Sketch010
  ReferenceAxis = -> Sketch010 [N_Axis]
  Refine = true
  Suppressed = false
  Type = 0
FEATURE [PartDesign::Fillet] Fillet002
  Base = -> Pocket005 [Edge3,Edge78,Edge86,Edge10]
  BaseFeature = -> Pocket005
  Radius = 1.5
  Refine = true
  SupportTransform = false
  Suppressed = false
  UseAllEdges = false
FEATURE [Sketcher::SketchObject] Sketch011
  ArcFitTolerance = 1e-06
  FullyConstrained = true
  MakeInternals = false
  MapMode = 5
  Placement = pos=(0,-105.6,0) rot=(0,0.707107,0.707107;3.14159rad)
  sketch-geometry (9):
    g0: LineSegment [constr] StartX=-12 StartY=43.14 StartZ=0 EndX=-12 EndY=10.2 EndZ=0
    g1: LineSegment StartX=-11 StartY=43.14 StartZ=0 EndX=-11 EndY=10.2 EndZ=0
    g2: LineSegment StartX=-10 StartY=43.14 StartZ=0 EndX=-10 EndY=10.2 EndZ=0
    g3: LineSegment StartX=-11 StartY=10.2 StartZ=0 EndX=-10 EndY=10.2 EndZ=0
    g4: LineSegment StartX=-11 StartY=43.14 StartZ=0 EndX=-10 EndY=43.14 EndZ=0
    g5: LineSegment StartX=-13 StartY=43.14 StartZ=0 EndX=-13 EndY=10.2 EndZ=0
    g6: LineSegment StartX=-14 StartY=43.14 StartZ=0 EndX=-14 EndY=10.2 EndZ=0
    g7: LineSegment StartX=-13 StartY=10.2 StartZ=0 EndX=-14 EndY=10.2 EndZ=0
    g8: LineSegment StartX=-13 StartY=43.14 StartZ=0 EndX=-14 EndY=43.14 EndZ=0
  constraints (25):
    c: Distance(g0) = 32.94
    c: Vertical(g0)
    c: PointOnObject(g0,g-3)
    c: Distance(g-2,g0) = 12
    c: PointOnObject(g1,g-3)
    c: Vertical(g1)
    c: PointOnObject(g2,g-3)
    c: Vertical(g2)
    c: Equal(g2,g0)
    c: Distance(g3) = 1
    c: Coincident(g3,g1)
    c: Perpendicular(g2,g3) = 1.5708
    c: Coincident(g4,g1)
    c: Coincident(g4,g2)
    c: Distance(g1,g0) = 1
    c: Vertical(g5)
    c: Vertical(g6)
    c: Distance(g7) = 1
    c: Coincident(g7,g5)
    c: Perpendicular(g6,g7) = 4.71239
    c: Coincident(g8,g5)
    c: Coincident(g8,g6)
    c: Symmetric(g1,g5,g0)
    c: Equal(g0,g1)
    c: Equal(g6,g0)
FEATURE [PartDesign::Pad] Pad005
  BaseFeature = -> Fillet002
  Direction = (0,1,-2e-16)
  Length = 0.63
  Length2 = 10
  Profile = -> Sketch011
  ReferenceAxis = -> Sketch011 [N_Axis]
  Refine = true
  Suppressed = false
  Type = 0
FEATURE [PartDesign::Mirrored] Mirrored005
  BaseFeature = -> Pad005
  MirrorPlane = -> YZ_Plane001
  Originals = -> [Pad005]
  Refine = true
  Suppressed = false
  TransformMode = 0
FEATURE [Sketcher::SketchObject] Sketch012
  ArcFitTolerance = 1e-06
  AttachmentSupport = -> [Mirrored005]
  ExternalGeometry = -> [Mirrored005]
  FullyConstrained = true
  MakeInternals = false
  MapMode = 5
  Placement = pos=(0,-1.4,0) rot=(1,0,0;1.5708rad)
  sketch-geometry (16):
    g0: LineSegment StartX=-14 StartY=43.14 StartZ=0 EndX=-13 EndY=43.14 EndZ=0
    g1: LineSegment StartX=-11 StartY=43.14 StartZ=0 EndX=-10 EndY=43.14 EndZ=0
    g2: LineSegment StartX=-14 StartY=43.14 StartZ=0 EndX=-14 EndY=10.2 EndZ=0
    g3: LineSegment StartX=-14 StartY=10.2 StartZ=0 EndX=-13 EndY=10.2 EndZ=0
    g4: LineSegment StartX=-13 StartY=10.2 StartZ=0 EndX=-13 EndY=43.14 EndZ=0
    g5: LineSegment StartX=-11 StartY=43.14 StartZ=0 EndX=-11 EndY=10.2 EndZ=0
    g6: LineSegment StartX=-11 StartY=10.2 StartZ=0 EndX=-10 EndY=10.2 EndZ=0
    g7: LineSegment StartX=-10 StartY=10.2 StartZ=0 EndX=-10 EndY=43.14 EndZ=0
    g8: LineSegment StartX=10 StartY=43.14 StartZ=0 EndX=11 EndY=43.14 EndZ=0
    g9: LineSegment StartX=10 StartY=43.14 StartZ=0 EndX=10 EndY=10.2 EndZ=0
    g10: LineSegment StartX=10 StartY=10.2 StartZ=0 EndX=11 EndY=10.2 EndZ=0
    g11: LineSegment StartX=11 StartY=10.2 StartZ=0 EndX=11 EndY=43.14 EndZ=0
    g12: LineSegment StartX=13 StartY=43.14 StartZ=0 EndX=14 EndY=43.14 EndZ=0
    g13: LineSegment StartX=13 StartY=43.14 StartZ=0 EndX=13 EndY=10.2 EndZ=0
    g14: LineSegment StartX=13 StartY=10.2 StartZ=0 EndX=14 EndY=10.2 EndZ=0
    g15: LineSegment StartX=14 StartY=10.2 StartZ=0 EndX=14 EndY=43.14 EndZ=0
  constraints (32):
    c: Coincident(g0,g-16)
    c: Coincident(g0,g-15)
    c: Coincident(g1,g-13)
    c: Coincident(g1,g-14)
    c: Coincident(g2,g0)
    c: Coincident(g2,g-18)
    c: Coincident(g3,g2)
    c: Coincident(g3,g-18)
    c: Coincident(g4,g3)
    c: Coincident(g4,g0)
    c: Coincident(g5,g1)
    c: Coincident(g5,g-17)
    c: Coincident(g6,g5)
    c: Coincident(g6,g-17)
    c: Coincident(g7,g6)
    c: Coincident(g7,g1)
    c: Coincident(g8,g-7)
    c: Coincident(g8,g-8)
    c: Coincident(g9,g8)
    c: Coincident(g9,g-10)
    c: Coincident(g10,g9)
    c: Coincident(g10,g-10)
    c: Coincident(g11,g10)
    c: Coincident(g11,g8)
    c: Coincident(g12,g-5)
    c: Coincident(g12,g-5)
    c: Coincident(g13,g12)
    c: Coincident(g13,g-9)
    c: Coincident(g14,g13)
    c: Coincident(g14,g-9)
    c: Coincident(g15,g14)
    c: Coincident(g15,g12)
FEATURE [PartDesign::Pad] Pad006
  BaseFeature = -> Mirrored005
  Direction = (0,-1,2e-16)
  Length = 0.63
  Length2 = 10
  Profile = -> Sketch012
  ReferenceAxis = -> Sketch012 [N_Axis]
  Refine = true
  Suppressed = false
  Type = 0
FEATURE [Sketcher::SketchObject] Sketch013
  ArcFitTolerance = 1e-06
  AttachmentSupport = -> [Pad006]
  ExternalGeometry = -> [Pad006]
  FullyConstrained = true
  MakeInternals = false
  MapMode = 5
  Placement = pos=(28.6,0,0) rot=(0.57735,-0.57735,-0.57735;2.0944rad)
  sketch-geometry (9):
    g0: LineSegment [constr] StartX=4.76 StartY=34.14 StartZ=0 EndX=4.76 EndY=19.14 EndZ=0
    g1: LineSegment StartX=2.76 StartY=34.14 StartZ=0 EndX=3.76 EndY=34.14 EndZ=0
    g2: LineSegment StartX=2.76 StartY=34.14 StartZ=0 EndX=2.76 EndY=19.14 EndZ=0
    g3: LineSegment StartX=3.76 StartY=34.14 StartZ=0 EndX=3.76 EndY=19.14 EndZ=0
    g4: LineSegment StartX=2.76 StartY=19.14 StartZ=0 EndX=3.76 EndY=19.14 EndZ=0
    g5: LineSegment StartX=6.76 StartY=34.14 StartZ=0 EndX=6.76 EndY=19.14 EndZ=0
    g6: LineSegment StartX=6.76 StartY=19.14 StartZ=0 EndX=5.76 EndY=19.14 EndZ=0
    g7: LineSegment StartX=5.76 StartY=34.14 StartZ=0 EndX=5.76 EndY=19.14 EndZ=0
    g8: LineSegment StartX=6.76 StartY=34.14 StartZ=0 EndX=5.76 EndY=34.14 EndZ=0
  constraints (27):
    c: Vertical(g0)
    c: PointOnObject(g0,g-3)
    c: Distance(g0,g-4) = 3.36
    c: Distance(g1) = 1
    c: Horizontal(g1)
    c: PointOnObject(g1,g-3)
    c: Vertical(g2)
    c: Coincident(g2,g1)
    c: Distance(g3) = 15
    c: Vertical(g3)
    c: Coincident(g3,g1)
    c: Coincident(g4,g2)
    c: Coincident(g4,g3)
    c: Equal(g0,g3)
    c: Equal(g3,g2)
    c: Distance(g0,g3) = 1
    c: Distance(g8) = 1
    c: Horizontal(g8)
    c: Vertical(g5)
    c: Coincident(g5,g8)
    c: Distance(g7) = 15
    c: Vertical(g7)
    c: Coincident(g7,g8)
    c: Coincident(g6,g5)
    c: Coincident(g6,g7)
    c: Equal(g7,g5)
    c: Symmetric(g6,g3,g0)
FEATURE [PartDesign::Pad] Pad007
  BaseFeature = -> Pad006
  Direction = (-1,0,0)
  Length = 2.66
  Length2 = 10
  Profile = -> Sketch013
  ReferenceAxis = -> Sketch013 [N_Axis]
  Refine = true
  Suppressed = false
  Type = 0
FEATURE [PartDesign::Plane] DatumPlane
  AttachmentOffset = pos=(0,0,53.5) rot=(0,0,1;0rad)
  AttachmentSupport = -> [Sketch013]
  Length = 91.037
  MapMode = 4
  Placement = pos=(28.6,-53.5,0) rot=(0.57735,-0.57735,0.57735;2.0944rad)
  ResizeMode = 0
  Width = 103.902
FEATURE [PartDesign::Mirrored] Mirrored006
  BaseFeature = -> Pad007
  MirrorPlane = -> DatumPlane
  Originals = -> [Pad007]
  Refine = true
  Suppressed = false
  TransformMode = 0
FEATURE [Sketcher::SketchObject] Sketch014
  ArcFitTolerance = 1e-06
  AttachmentSupport = -> [Mirrored006]
  ExternalGeometry = -> [Mirrored006]
  FullyConstrained = true
  MakeInternals = false
  MapMode = 5
  Placement = pos=(-28.6,0,0) rot=(0.57735,0.57735,0.57735;2.0944rad)
  sketch-geometry (16):
    g0: LineSegment StartX=-104.24 StartY=34.14 StartZ=0 EndX=-103.24 EndY=34.14 EndZ=0
    g1: LineSegment StartX=-104.24 StartY=34.14 StartZ=0 EndX=-104.24 EndY=19.14 EndZ=0
    g2: LineSegment StartX=-104.24 StartY=19.14 StartZ=0 EndX=-103.24 EndY=19.14 EndZ=0
    g3: LineSegment StartX=-103.24 StartY=19.14 StartZ=0 EndX=-103.24 EndY=34.14 EndZ=0
    g4: LineSegment StartX=-101.24 StartY=34.14 StartZ=0 EndX=-100.24 EndY=34.14 EndZ=0
    g5: LineSegment StartX=-101.24 StartY=34.14 StartZ=0 EndX=-101.24 EndY=19.14 EndZ=0
    g6: LineSegment StartX=-101.24 StartY=19.14 StartZ=0 EndX=-100.24 EndY=19.14 EndZ=0
    g7: LineSegment StartX=-100.24 StartY=19.14 StartZ=0 EndX=-100.24 EndY=34.14 EndZ=0
    g8: LineSegment StartX=-6.76 StartY=34.14 StartZ=0 EndX=-5.76 EndY=34.14 EndZ=0
    g9: LineSegment StartX=-6.76 StartY=34.14 StartZ=0 EndX=-6.76 EndY=19.14 EndZ=0
    g10: LineSegment StartX=-6.76 StartY=19.14 StartZ=0 EndX=-5.76 EndY=19.14 EndZ=0
    g11: LineSegment StartX=-5.76 StartY=19.14 StartZ=0 EndX=-5.76 EndY=34.14 EndZ=0
    g12: LineSegment StartX=-3.76 StartY=34.14 StartZ=0 EndX=-2.76 EndY=34.14 EndZ=0
    g13: LineSegment StartX=-3.76 StartY=34.14 StartZ=0 EndX=-3.76 EndY=19.14 EndZ=0
    g14: LineSegment StartX=-3.76 StartY=19.14 StartZ=0 EndX=-2.76 EndY=19.14 EndZ=0
    g15: LineSegment StartX=-2.76 StartY=19.14 StartZ=0 EndX=-2.76 EndY=34.14 EndZ=0
  constraints (32):
    c: Coincident(g0,g-6)
    c: Coincident(g0,g-6)
    c: Coincident(g1,g0)
    c: Coincident(g1,g-5)
    c: Coincident(g2,g1)
    c: Coincident(g2,g-4)
    c: Coincident(g3,g2)
    c: Coincident(g3,g0)
    c: Coincident(g4,g-9)
    c: Coincident(g4,g-8)
    c: Coincident(g5,g4)
    c: Coincident(g5,g-10)
    c: Coincident(g6,g5)
    c: Coincident(g6,g-10)
    c: Coincident(g7,g6)
    c: Coincident(g7,g4)
    c: Coincident(g8,g-14)
    c: Coincident(g8,g-14)
    c: Coincident(g9,g8)
    c: Coincident(g9,g-13)
    c: Coincident(g10,g9)
    c: Coincident(g10,g-12)
    c: Coincident(g11,g10)
    c: Coincident(g11,g8)
    c: Coincident(g12,g-17)
    c: Coincident(g12,g-16)
    c: Coincident(g13,g12)
    c: Coincident(g13,g-18)
    c: Coincident(g14,g13)
    c: Coincident(g14,g-18)
    c: Coincident(g15,g14)
    c: Coincident(g15,g12)
FEATURE [PartDesign::Pad] Pad008
  BaseFeature = -> Mirrored006
  Direction = (1,0,0)
  Length = 2.66
  Length2 = 10
  Profile = -> Sketch014
  ReferenceAxis = -> Sketch014 [N_Axis]
  Refine = true
  Suppressed = false
  Type = 0
FEATURE [PartDesign::Fillet] Fillet003
  Base = -> Pad008 [Edge379,Edge371,Edge373]
  BaseFeature = -> Pad008
  Radius = 2
  Refine = true
  SupportTransform = false
  Suppressed = false
  UseAllEdges = false
FEATURE [PartDesign::Body] Body001
  AllowCompound = false
  Group = -> [Sketch,Pad,Thickness,Thickness001,Sketch001,Pocket,Sketch002,Pad001,Sketch003,Pad002,Sketch004,Pad003,Sketch005,Pad004,Mirrored,Sketch006,Pocket001,Mirrored001,Sketch007,Pocket002,Mirrored002,Fillet,Mirrored003,Sketch008,Pocket003,Sketch009,Pocket004,Mirrored004,Fillet001,Sketch010,Pocket005,Fillet002,Sketch011,Pad005,Mirrored005,Sketch012,Pad006,Sketch013,Pad007,DatumPlane,Mirrored006,Sketch014,+2 more]
  Origin = -> Origin001
  Tip = -> Fillet003
